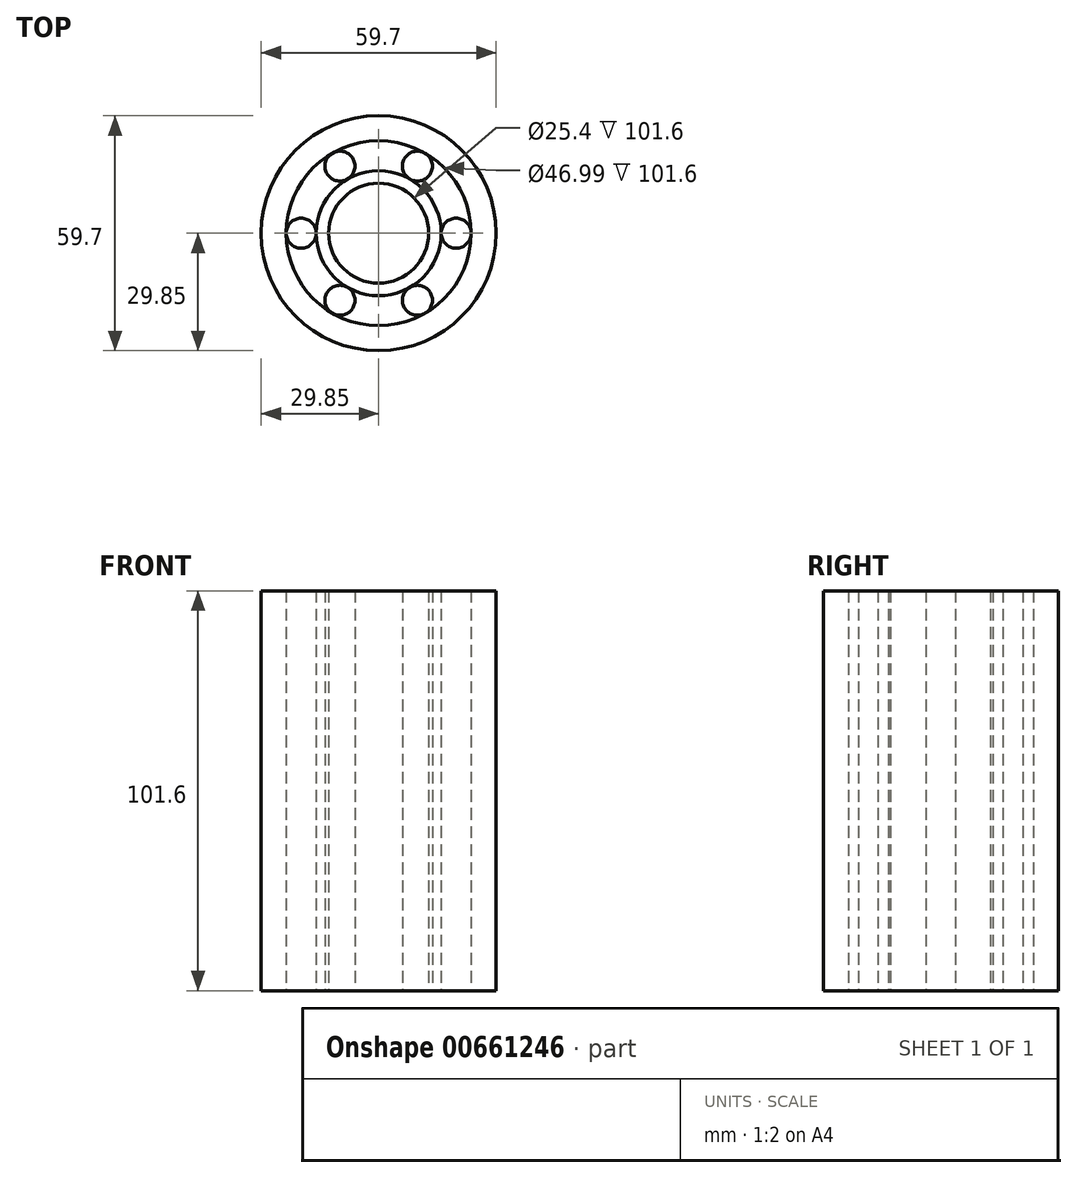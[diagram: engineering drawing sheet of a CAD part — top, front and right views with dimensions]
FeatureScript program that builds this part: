
annotation { "Feature Type Name" : "Feature", "Feature Type Description" : "" }
export const myFeature = defineFeature(function(context is Context, id is Id, definition is map)
    precondition{}
    {
        {
            var Q0;
            Q0=qCreatedBy(makeId("Top.planeOp"),FACE);
            var sketch = newSketch(context, id + "F0", { "sketchPlane" : qUnion([Q0])});
            skCircle(sketch, "E0", {"center": v(0, 0) * mm, "radius": 12.7 * mm});
            skCircle(sketch, "E1", {"center": v(0, 0) * mm, "radius": 15.88 * mm});
            skCircle(sketch, "E2", {"center": v(-19.69, 0) * mm, "radius": 3.81 * mm});
            skCircle(sketch, "E3.1.0", {"center": v(-9.84, 17.05) * mm, "radius": 3.81 * mm});
            skCircle(sketch, "E3.2.0", {"center": v(9.84, 17.05) * mm, "radius": 3.81 * mm});
            skCircle(sketch, "E3.3.0", {"center": v(19.69, 0) * mm, "radius": 3.81 * mm});
            skCircle(sketch, "E3.4.0", {"center": v(9.84, -17.05) * mm, "radius": 3.81 * mm});
            skCircle(sketch, "E3.5.0", {"center": v(-9.84, -17.05) * mm, "radius": 3.81 * mm});
            skLineSegment(sketch, "E3.anchor1", {"start": v(0, 0) * mm, "end": v(-19.69, 0) * mm, "construction": true});
            skLineSegment(sketch, "E3.anchor2", {"start": v(0, 0) * mm, "end": v(-9.84, -17.05) * mm, "construction": true});
            skCircle(sketch, "E4", {"center": v(0, 0) * mm, "radius": 23.5 * mm});
            skCircle(sketch, "E5", {"center": v(0, 0) * mm, "radius": 29.85 * mm});
            skSolve(sketch);
        }
        {
            var Q0;
            Q0 = qSketchRegion(id + "F0", true);
            var Q1;
            {var subQ0=sQuery(id+"F0.wireOp",EDGE,"E3.1.0");var subQ1=makeQuery(id+"F0.imprint","INTERSECT",VERTEX,{"derivedFrom":[sQuery(id+"F0.wireOp",EDGE,"E1"),subQ0]});Q1=makeQuery(id+"F0.imprint","IMPRINT",FACE,{"disambiguationData":[TD([[makeQuery(id+"F0.imprint","IMPRINT",EDGE,{"disambiguationData":[TD([[subQ1,-1.0]])],"derivedFrom":subQ0}),1.0]])]});}
            var Q2;
            {var subQ0=sQuery(id+"F0.wireOp",EDGE,"E3.2.0");var subQ1=makeQuery(id+"F0.imprint","INTERSECT",VERTEX,{"derivedFrom":[sQuery(id+"F0.wireOp",EDGE,"E1"),subQ0]});Q2=makeQuery(id+"F0.imprint","IMPRINT",FACE,{"disambiguationData":[TD([[makeQuery(id+"F0.imprint","IMPRINT",EDGE,{"disambiguationData":[TD([[subQ1,-1.0]])],"derivedFrom":subQ0}),1.0]])]});}
            var Q3;
            {var subQ0=sQuery(id+"F0.wireOp",EDGE,"E3.3.0");var subQ1=makeQuery(id+"F0.imprint","INTERSECT",VERTEX,{"derivedFrom":[sQuery(id+"F0.wireOp",EDGE,"E1"),subQ0]});Q3=makeQuery(id+"F0.imprint","IMPRINT",FACE,{"disambiguationData":[TD([[makeQuery(id+"F0.imprint","IMPRINT",EDGE,{"disambiguationData":[TD([[subQ1,-1.0]])],"derivedFrom":subQ0}),1.0]])]});}
            var Q4;
            {var subQ0=sQuery(id+"F0.wireOp",EDGE,"E3.4.0");var subQ1=makeQuery(id+"F0.imprint","INTERSECT",VERTEX,{"derivedFrom":[sQuery(id+"F0.wireOp",EDGE,"E1"),subQ0]});Q4=makeQuery(id+"F0.imprint","IMPRINT",FACE,{"disambiguationData":[TD([[makeQuery(id+"F0.imprint","IMPRINT",EDGE,{"disambiguationData":[TD([[subQ1,-1.0]])],"derivedFrom":subQ0}),1.0]])]});}
            var Q5;
            {var subQ0=sQuery(id+"F0.wireOp",EDGE,"E3.5.0");var subQ1=makeQuery(id+"F0.imprint","INTERSECT",VERTEX,{"derivedFrom":[sQuery(id+"F0.wireOp",EDGE,"E1"),subQ0]});Q5=makeQuery(id+"F0.imprint","IMPRINT",FACE,{"disambiguationData":[TD([[makeQuery(id+"F0.imprint","IMPRINT",EDGE,{"disambiguationData":[TD([[subQ1,-1.0]])],"derivedFrom":subQ0}),1.0]])]});}
            var Q6;
            {var subQ0=sQuery(id+"F0.wireOp",EDGE,"E2");var subQ1=makeQuery(id+"F0.imprint","INTERSECT",VERTEX,{"derivedFrom":[sQuery(id+"F0.wireOp",EDGE,"E1"),subQ0]});Q6=makeQuery(id+"F0.imprint","IMPRINT",FACE,{"disambiguationData":[TD([[makeQuery(id+"F0.imprint","IMPRINT",EDGE,{"disambiguationData":[TD([[subQ1,-1.0]])],"derivedFrom":subQ0}),1.0]])]});}
            var Q7;
            Q7=makeQuery(id+"F0.imprint","IMPRINT",FACE,{"disambiguationData":[TD([[makeQuery(id+"F0.imprint","IMPRINT",EDGE,{"derivedFrom":sQuery(id+"F0.wireOp",EDGE,"E0")}),-1.0]])]});
            extrude(context, id + "F1", {"entities" : qUnion([Q0, Q1, Q2, Q3, Q4, Q5, Q6, Q7]), "depth" : 101.6 * mm, "offsetDistance" : 25.4 * mm});
        }
    });
